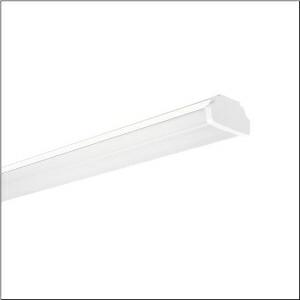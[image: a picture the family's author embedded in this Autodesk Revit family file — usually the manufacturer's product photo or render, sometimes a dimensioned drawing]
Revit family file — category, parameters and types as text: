
# Revit family: modario_r__31_mo_53bm81271v4080_0fb4
name_source: partatom
category: Lighting Fixtures
units: mm (PartAtom-declared; Revit-internal decimal feet)

## family parameters
Cut with Voids When Loaded = No
Host = Face
Light Source = No
Part Type = Normal
Room Calculation Point = No
Round Connector Dimension = Use Diameter
Shared = No

## types (1)
- Modario® 31 MO (1 x LED, 7810 lm, 50.8 W, 4000K)
    Apparent Load = 51 VA
    CIE Flux Codes = 47 80 95 92 100
    Color Rendering = 80
    Color Temperature = 4000K
    Default Elevation = 1800 mm
    Description = Modario® 31 MOluminaire insert, length: 1.495mm, width: 81mm, height: 82mm, LED rated luminous flux: 7.810lm, light colour: 840, control gear: ON/OFF, control gear: ECG, with plug, 3-pole, with phase selection, mains connection: 220..240V, AC, 50/60Hz, primary optical cover: cover, of PMMA, light emission: direct distribution, primary light characteristic: symmetric, protection rating (complete): IP20, protection rating (LED compartment): IP50, insulation class (complete): insulation class I (protective earthing), certification: CE, ENEC, VDE, permissible ambient temperature for indoor applications: -35..+35°C, corresponds to IFS (International Featured Standards) requirements for safety and quality in the food industry, reducing of maximum allowable ambient temperature of 5°C with ceiling mounting, packaging unit: 1 piece
    Height = 92 mm
    Lamp = 1 x LED
    Lamp Light Flux = 7810 lm
    Lamp Power = 50.8 W
    Lamp count = 1
    Length = 1495 mm
    Luminous efficacy = 154 lm/W
    Manufacturer = Siteco
    ModVariant = No
    Model = 53BM81271V4080
    Mounting Place = Ceiling
    Mounting Type = Pendant
    Number of Poles = 1
    OnlyDefault = Yes
    Power Factor = 1
    Product Name = Modario® 31 MO
    Product group = luminaire insert
    ProductGroupID = 902
    Protection Class = Protection class I
    Protection Degree = IP 20
    RLX_Detail_Level = 1
    RlxData = <blob elided: 38393 chars, md5=74aff6d7>
    Socket = socket
    Standby Power = 0 W
    System Light Flux = 7810 lm
    System Power = 51 W
    Type Comments = Product without accessories
    Type Image = l_1003447.jpg
    URL = http://relux.com
    VarID = ---
    Voltage = 0 V
    Weight = 0.00 kg
    Width = 81 mm

## geometry (parser evidence)
native form markers: Blend x4, Sweep x12
no freeform markers — native parametric forms only
